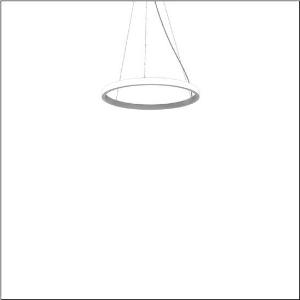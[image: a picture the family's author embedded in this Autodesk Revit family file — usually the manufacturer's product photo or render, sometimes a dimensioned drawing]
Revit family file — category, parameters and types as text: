
# Revit family: silica_r__21_ring-o_5pjbo1d3204a_6aba
name_source: partatom
category: Lighting Fixtures
units: mm (PartAtom-declared; Revit-internal decimal feet)

## family parameters
Cut with Voids When Loaded = No
Host = Face
Light Source = No
Part Type = Normal
Room Calculation Point = No
Round Connector Dimension = Use Diameter
Shared = No

## types (1)
- Silica® 21 Ring-O (1 x LED, 3930 lm, 60 W, 4000K)
    Apparent Load = 60 VA
    CIE Flux Codes = 2 16 49 50 100
    Color Rendering = 80
    Color Temperature = 4000K
    Default Elevation = 1800 mm
    Description = Silica® 21 Ring-O, suspended luminaire, of PMMA, frosted, light emission: outer ring side luminous distribution, primary light characteristic: symmetric, installation type: suspended mounting, LED, rated luminous flux: 3.930lm, luminous efficacy: 66lm/W, light colour: 840, colour temperature: 4000K, with terminal, 5-pole, mains connection: 230V, AC/DC, 0/50..60Hz, rated input power: 60W, housing, of extruded aluminium section, metallic grey (RAL 9006), diameter: 610mm, ceiling canopy, metallic grey (RAL 9006), protection rating (lamp compartment): IP40, insulation class (complete): insulation class I (protective earthing), certification: CE, impact resistance: IK02, permissible operating ambient temperature: 0..+35°C, packaging unit: 1 piece
    Height = 48 mm  [stored 0.15748 ft]
    Lamp = 1 x LED
    Lamp Light Flux = 3930 lm
    Lamp Power = 60 W
    Lamp count = 1
    Length = 610 mm
    Luminous efficacy = 66 lm/W
    Manufacturer = Siteco
    ModVariant = No
    Model = 5PJBO1D3204A
    Mounting Place = Ceiling
    Mounting Type = Pendant
    Number of Poles = 1
    OnlyDefault = Yes
    Power Factor = 1
    Product Name = Silica® 21 Ring-O
    Product group = suspended luminaire
    ProductGroupID = 904
    Protection Class = Protection class I
    Protection Degree = IP 40
    RLX_Detail_Level = 1
    RLX_Emergency_Light_Flux = 0 lm
    RLX_Emergency_Type = 0
    RLX_Emergency_Type_DB = No
    RlxData = <blob elided: 11621 chars, md5=5c3d78d2>
    Socket = socket
    Standby Power = 0 W
    System Light Flux = 3930 lm
    System Power = 60 W
    Type Comments = Product without accessories
    Type Image = l_1251758.jpg
    URL = http://relux.com
    VarID = ---
    Voltage = 0 V
    Weight = 0.00 kg
    Width = 0 mm  [stored 0 ft]

note: [stored X ft] marks values corroborated as IEEE doubles in the binary element streams (Revit-internal decimal feet)

## geometry (parser evidence)
native form markers: Sweep x13
no freeform markers — native parametric forms only
